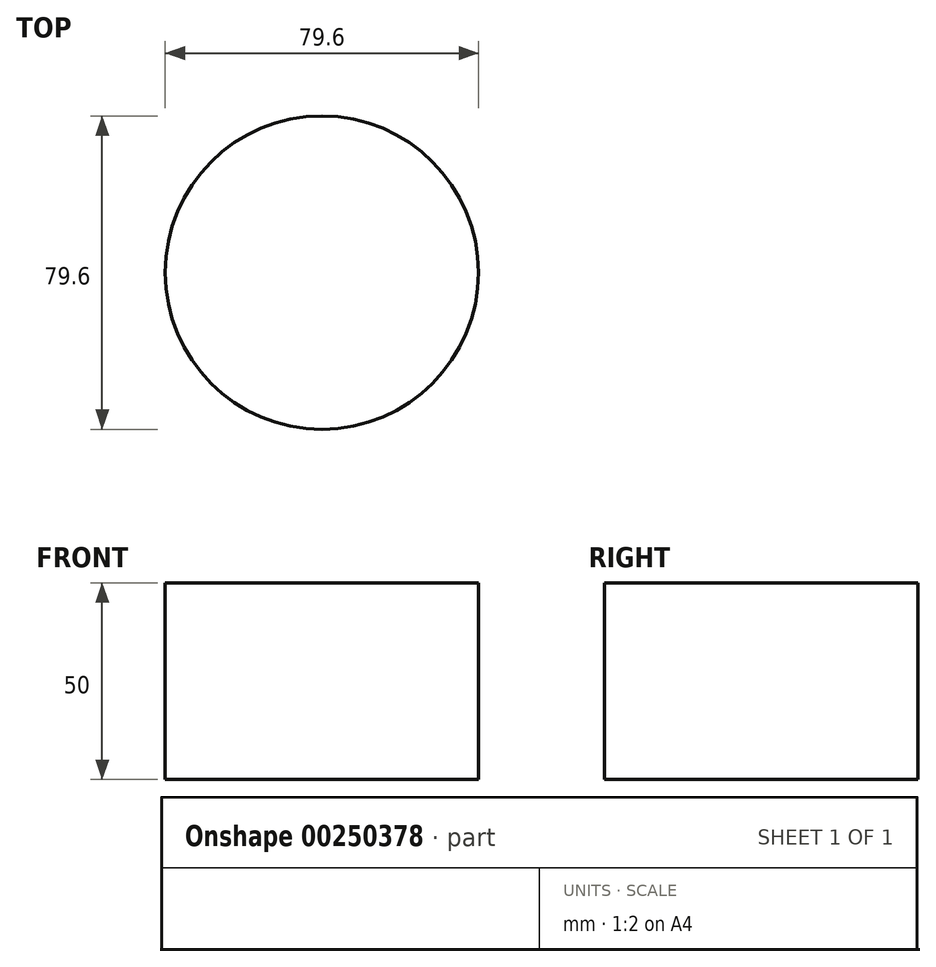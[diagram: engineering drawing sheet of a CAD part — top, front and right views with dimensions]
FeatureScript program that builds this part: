
annotation { "Feature Type Name" : "Feature", "Feature Type Description" : "" }
export const myFeature = defineFeature(function(context is Context, id is Id, definition is map)
    precondition{}
    {
        {
            var Q0;
            Q0=qCreatedBy(makeId("Top.planeOp"),FACE);
            var sketch = newSketch(context, id + "F0", { "sketchPlane" : qUnion([Q0])});
            skCircle(sketch, "E0", {"center": v(0, 0) * mm, "radius": 39.8 * mm});
            skSolve(sketch);
        }
        {
            var Q0;
            Q0 = qSketchRegion(id + "F0", true);
            extrude(context, id + "F1", {"entities" : qUnion([Q0]), "depth" : 50 * mm});
        }
    });
